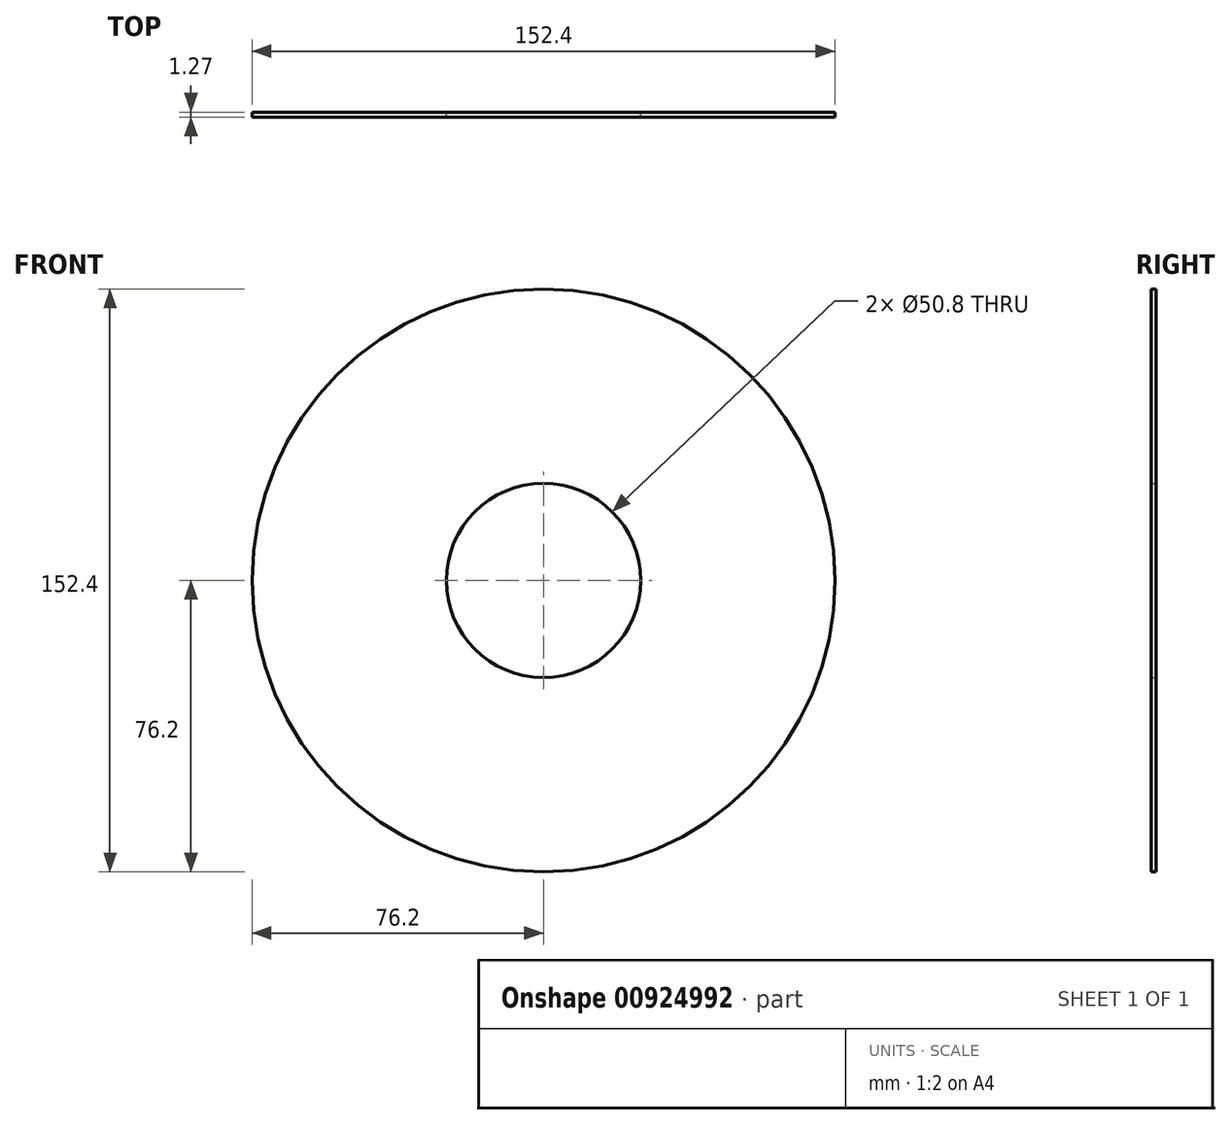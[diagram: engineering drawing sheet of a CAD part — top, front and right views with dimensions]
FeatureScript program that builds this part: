
annotation { "Feature Type Name" : "Feature", "Feature Type Description" : "" }
export const myFeature = defineFeature(function(context is Context, id is Id, definition is map)
    precondition{}
    {
        {
            var Q0;
            Q0=qCreatedBy(makeId("Front.planeOp"),FACE);
            var sketch = newSketch(context, id + "F0", { "sketchPlane" : qUnion([Q0])});
            skCircle(sketch, "E0", {"center": v(0, 0) * mm, "radius": 76.2 * mm});
            skCircle(sketch, "E1", {"center": v(0, 0) * mm, "radius": 25.4 * mm});
            skSolve(sketch);
        }
        {
            var Q0;
            Q0=makeQuery(id+"F0.imprint","IMPRINT",FACE,{"disambiguationData":[TD([[makeQuery(id+"F0.imprint","IMPRINT",EDGE,{"derivedFrom":sQuery(id+"F0.wireOp",EDGE,"E0")}),1.0]])]});
            extrude(context, id + "F1", {"entities" : qUnion([Q0]), "depth" : 1.27 * mm, "offsetDistance" : 25.4 * mm});
        }
        {
            var Q0;
            Q0 = qSketchRegion(id + "F0", true);
            extrude(context, id + "F2", {"entities" : qUnion([Q0]), "depth" : 1.27 * mm, "offsetDistance" : 25.4 * mm});
        }
    });
